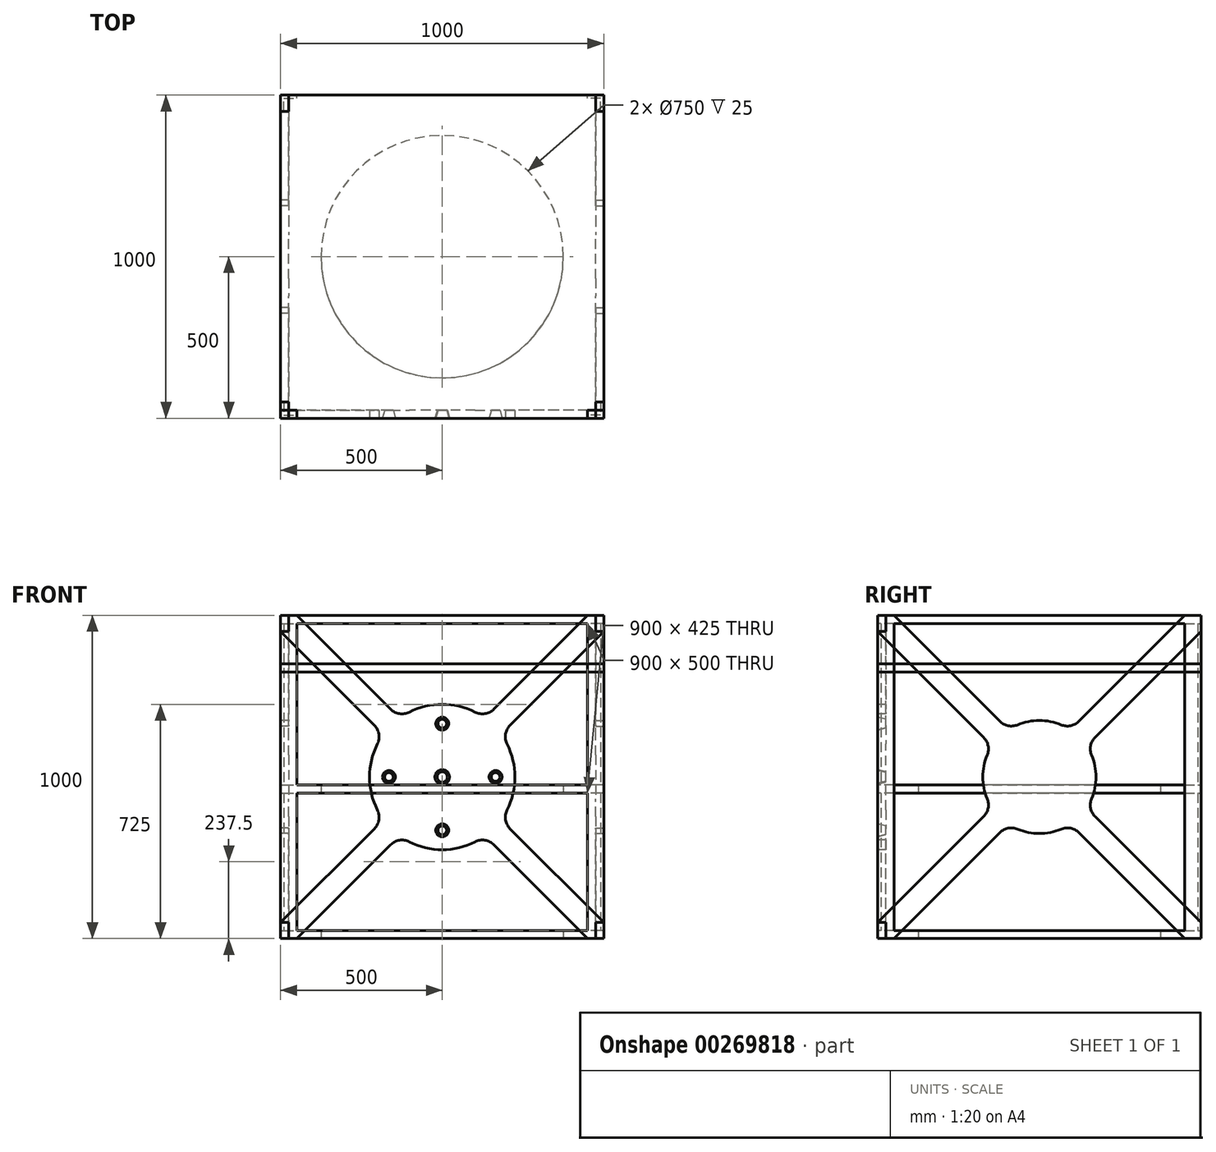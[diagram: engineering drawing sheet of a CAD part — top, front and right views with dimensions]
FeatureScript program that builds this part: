
annotation { "Feature Type Name" : "Feature", "Feature Type Description" : "" }
export const myFeature = defineFeature(function(context is Context, id is Id, definition is map)
    precondition{}
    {
        {
            var Q0;
            Q0=qCreatedBy(makeId("Top.planeOp"),FACE);
            var sketch = newSketch(context, id + "F0", { "sketchPlane" : qUnion([Q0])});
            skLineSegment(sketch, "E0.bottom", {"start": v(0, 0) * mm, "end": v(1000, 0) * mm});
            skLineSegment(sketch, "E0.top", {"start": v(0, -1000) * mm, "end": v(1000, -1000) * mm});
            skLineSegment(sketch, "E0.left", {"start": v(0, 0) * mm, "end": v(0, -1000) * mm});
            skLineSegment(sketch, "E0.right", {"start": v(1000, 0) * mm, "end": v(1000, -1000) * mm});
            skSolve(sketch);
        }
        {
            var Q0;
            Q0 = qSketchRegion(id + "F0", true);
            extrude(context, id + "F1", {"entities" : qUnion([Q0]), "depth" : 25 * mm});
        }
        {
            var Q0;
            Q0=makeQuery(id+"F1.opExtrude","CAP_FACE",FACE,{"disambiguationData":[OSD([sQuery(id+"F0.wireOp",EDGE,"E0.bottom"),sQuery(id+"F0.wireOp",EDGE,"E0.top"),sQuery(id+"F0.wireOp",EDGE,"E0.left"),sQuery(id+"F0.wireOp",EDGE,"E0.right")])],"isStart":false});
            var sketch = newSketch(context, id + "F2", { "sketchPlane" : qUnion([Q0])});
            skLineSegment(sketch, "E1", {"start": v(0, -1000) * mm, "end": v(0, -950) * mm});
            skLineSegment(sketch, "E2", {"start": v(0, -950) * mm, "end": v(10, -950) * mm});
            skLineSegment(sketch, "E3", {"start": v(10, -950) * mm, "end": v(10, -990) * mm});
            skLineSegment(sketch, "E4", {"start": v(10, -990) * mm, "end": v(50, -990) * mm});
            skLineSegment(sketch, "E5", {"start": v(50, -990) * mm, "end": v(50, -1000) * mm});
            skLineSegment(sketch, "E6", {"start": v(50, -1000) * mm, "end": v(0, -1000) * mm});
            skLineSegment(sketch, "E7", {"start": v(0, -500) * mm, "end": v(1000, -500) * mm, "construction": true});
            skLineSegment(sketch, "E8.MirrorCS", {"start": v(50, 0) * mm, "end": v(0, 0) * mm});
            skLineSegment(sketch, "E9.MirrorCS", {"start": v(50, -10) * mm, "end": v(50, 0) * mm});
            skLineSegment(sketch, "E10.MirrorCS", {"start": v(10, -10) * mm, "end": v(50, -10) * mm});
            skLineSegment(sketch, "E11.MirrorCS", {"start": v(10, -50) * mm, "end": v(10, -10) * mm});
            skLineSegment(sketch, "E12.MirrorCS", {"start": v(0, -50) * mm, "end": v(10, -50) * mm});
            skLineSegment(sketch, "E13.MirrorCS", {"start": v(0, 0) * mm, "end": v(0, -50) * mm});
            skLineSegment(sketch, "E14", {"start": v(500, 0) * mm, "end": v(500, -1000) * mm, "construction": true});
            skLineSegment(sketch, "E15.MirrorCS", {"start": v(950, -990) * mm, "end": v(950, -1000) * mm});
            skLineSegment(sketch, "E16.MirrorCS", {"start": v(990, -990) * mm, "end": v(950, -990) * mm});
            skLineSegment(sketch, "E17.MirrorCS", {"start": v(990, -950) * mm, "end": v(990, -990) * mm});
            skLineSegment(sketch, "E18.MirrorCS", {"start": v(1000, -950) * mm, "end": v(990, -950) * mm});
            skLineSegment(sketch, "E19.MirrorCS", {"start": v(1000, -1000) * mm, "end": v(1000, -950) * mm});
            skLineSegment(sketch, "E20.MirrorCS", {"start": v(950, -1000) * mm, "end": v(1000, -1000) * mm});
            skLineSegment(sketch, "E21.MirrorCS", {"start": v(1000, 0) * mm, "end": v(1000, -50) * mm});
            skLineSegment(sketch, "E22.MirrorCS", {"start": v(990, -10) * mm, "end": v(950, -10) * mm});
            skLineSegment(sketch, "E23.MirrorCS", {"start": v(950, 0) * mm, "end": v(1000, 0) * mm});
            skLineSegment(sketch, "E24.MirrorCS", {"start": v(1000, -50) * mm, "end": v(990, -50) * mm});
            skLineSegment(sketch, "E25.MirrorCS", {"start": v(990, -50) * mm, "end": v(990, -10) * mm});
            skLineSegment(sketch, "E26.MirrorCS", {"start": v(950, -10) * mm, "end": v(950, 0) * mm});
            skSolve(sketch);
        }
        {
            var Q0;
            Q0 = qSketchRegion(id + "F2", true);
            extrude(context, id + "F3", {"entities" : qUnion([Q0]), "operationType" : NewBodyOperationType.ADD, "depth" : 950 * mm});
        }
        {
            var Q0;
            Q0=qCreatedBy(makeId("Top.planeOp"),FACE);
            cPlane(context, id + "F4", {"entities" : qUnion([Q0]), "cplaneType" : CPlaneType.OFFSET, "offset" : 450 * mm, "width" : 150 * mm, "height" : 150 * mm});
        }
        {
            var Q0;
            Q0=qCreatedBy(id+"F4.planeOp",FACE);
            var sketch = newSketch(context, id + "F5", { "sketchPlane" : qUnion([Q0])});
            skLineSegment(sketch, "E27.bottom", {"start": v(0, 0) * mm, "end": v(998.65, 0) * mm});
            skLineSegment(sketch, "E27.top", {"start": v(0, -1000) * mm, "end": v(998.65, -1000) * mm});
            skLineSegment(sketch, "E27.left", {"start": v(0, 0) * mm, "end": v(0, -1000) * mm});
            skLineSegment(sketch, "E27.right", {"start": v(998.65, 0) * mm, "end": v(998.65, -1000) * mm});
            skSolve(sketch);
        }
        {
            var Q0;
            Q0 = qSketchRegion(id + "F5", true);
            extrude(context, id + "F6", {"entities" : qUnion([Q0]), "operationType" : NewBodyOperationType.ADD, "depth" : 25 * mm});
        }
        {
            var Q0;
            Q0=qCreatedBy(id+"F4.planeOp",FACE);
            cPlane(context, id + "F7", {"entities" : qUnion([Q0]), "cplaneType" : CPlaneType.OFFSET, "offset" : 400 * mm, "width" : 150 * mm, "height" : 150 * mm});
        }
        {
            var Q0;
            Q0=qCreatedBy(id+"F7.planeOp",FACE);
            var sketch = newSketch(context, id + "F8", { "sketchPlane" : qUnion([Q0])});
            skLineSegment(sketch, "E28.bottom", {"start": v(0, 0) * mm, "end": v(1000, 0) * mm});
            skLineSegment(sketch, "E28.top", {"start": v(0, -1000) * mm, "end": v(1000, -1000) * mm});
            skLineSegment(sketch, "E28.left", {"start": v(0, 0) * mm, "end": v(0, -1000) * mm});
            skLineSegment(sketch, "E28.right", {"start": v(1000, 0) * mm, "end": v(1000, -1000) * mm});
            skSolve(sketch);
        }
        {
            var Q0;
            Q0 = qSketchRegion(id + "F8", true);
            extrude(context, id + "F9", {"entities" : qUnion([Q0]), "oppositeDirection" : true, "depth" : 25 * mm});
        }
        {
            var Q0;
            Q0=makeQuery(id+"F3.opExtrude","CAP_FACE",FACE,{"disambiguationData":[OSD([sQuery(id+"F2.wireOp",EDGE,"E8.MirrorCS"),sQuery(id+"F2.wireOp",EDGE,"E9.MirrorCS"),sQuery(id+"F2.wireOp",EDGE,"E10.MirrorCS"),sQuery(id+"F2.wireOp",EDGE,"E11.MirrorCS"),sQuery(id+"F2.wireOp",EDGE,"E12.MirrorCS"),sQuery(id+"F2.wireOp",EDGE,"E13.MirrorCS")])],"isStart":false});
            var sketch = newSketch(context, id + "F10", { "sketchPlane" : qUnion([Q0])});
            skLineSegment(sketch, "E29.bottom", {"start": v(0, 0) * mm, "end": v(1000, 0) * mm});
            skLineSegment(sketch, "E29.top", {"start": v(0, -1000) * mm, "end": v(1000, -1000) * mm});
            skLineSegment(sketch, "E29.left", {"start": v(0, 0) * mm, "end": v(0, -1000) * mm});
            skLineSegment(sketch, "E29.right", {"start": v(1000, 0) * mm, "end": v(1000, -1000) * mm});
            skSolve(sketch);
        }
        {
            var Q0;
            Q0 = qSketchRegion(id + "F10", true);
            extrude(context, id + "F11", {"entities" : qUnion([Q0]), "operationType" : NewBodyOperationType.ADD, "depth" : 25 * mm});
        }
        {
            var Q0;
            Q0=makeQuery(id+"F1.opExtrude","CAP_FACE",FACE,{"disambiguationData":[OSD([sQuery(id+"F0.wireOp",EDGE,"E0.bottom"),sQuery(id+"F0.wireOp",EDGE,"E0.top"),sQuery(id+"F0.wireOp",EDGE,"E0.left"),sQuery(id+"F0.wireOp",EDGE,"E0.right")])],"isStart":true});
            var sketch = newSketch(context, id + "F12", { "sketchPlane" : qUnion([Q0])});
            skCircle(sketch, "E30", {"center": v(500, 500) * mm, "radius": 375 * mm});
            skSolve(sketch);
        }
        {
            var Q0;
            Q0 = qSketchRegion(id + "F12", true);
            extrude(context, id + "F13", {"entities" : qUnion([Q0]), "operationType" : NewBodyOperationType.REMOVE, "oppositeDirection" : true, "depth" : 592 * mm});
        }
        {
            var Q0;
            Q0=makeQuery(id+"F11.boolean.opBoolean","MERGE",FACE,{"derivedFrom":[makeQuery(id+"F6.boolean.opBoolean","MERGE",FACE,{"derivedFrom":[makeQuery(id+"F3.boolean.opBoolean","MERGE",FACE,{"derivedFrom":[makeQuery(id+"F1.opExtrude","SWEPT_FACE",FACE,{"disambiguationData":[OSD([sQuery(id+"F0.wireOp",EDGE,"E0.top")])]}),makeQuery(id+"F3.opExtrude","SWEPT_FACE",FACE,{"disambiguationData":[OSD([sQuery(id+"F2.wireOp",EDGE,"E6")])]}),makeQuery(id+"F3.opExtrude","SWEPT_FACE",FACE,{"disambiguationData":[OSD([sQuery(id+"F2.wireOp",EDGE,"E20.MirrorCS")])]})]}),makeQuery(id+"F6.opExtrude","SWEPT_FACE",FACE,{"disambiguationData":[OSD([sQuery(id+"F5.wireOp",EDGE,"E27.top")])]})]}),makeQuery(id+"F11.opExtrude","SWEPT_FACE",FACE,{"disambiguationData":[OSD([sQuery(id+"F10.wireOp",EDGE,"E29.top")])]})]});
            var sketch = newSketch(context, id + "F14", { "sketchPlane" : qUnion([Q0])});
            skLineSegment(sketch, "E31", {"start": v(1000, 0) * mm, "end": v(1000, 50) * mm});
            skLineSegment(sketch, "E32", {"start": v(1000, 50) * mm, "end": v(709.85, 340.15) * mm});
            skLineSegment(sketch, "E33", {"start": v(0, 1000) * mm, "end": v(0, 950) * mm});
            skLineSegment(sketch, "E34", {"start": v(0, 950) * mm, "end": v(290.15, 659.85) * mm});
            skLineSegment(sketch, "E35", {"start": v(1000, 0) * mm, "end": v(950, 0) * mm});
            skLineSegment(sketch, "E36", {"start": v(50, 1000) * mm, "end": v(0, 1000) * mm});
            skLineSegment(sketch, "E37", {"start": v(1000, 1000) * mm, "end": v(950, 1000) * mm});
            skLineSegment(sketch, "E38", {"start": v(950, 1000) * mm, "end": v(659.85, 709.85) * mm});
            skLineSegment(sketch, "E39", {"start": v(0, 50) * mm, "end": v(0, 0) * mm});
            skLineSegment(sketch, "E40", {"start": v(0, 0) * mm, "end": v(50, 0) * mm});
            skLineSegment(sketch, "E41", {"start": v(50, 0) * mm, "end": v(340.15, 290.15) * mm});
            skLineSegment(sketch, "E42", {"start": v(1000, 950) * mm, "end": v(1000, 1000) * mm});
            skPoint(sketch, "E43.centerSnap0", {"position": v(500, 475) * mm});
            skArc(sketch, "E44", {"start": v(299.38, 601.86) * mm, "mid": v(275, 500) * mm, "end": v(299.38, 398.14) * mm});
            skLineSegment(sketch, "E45.trimOffspring", {"start": v(290.15, 340.15) * mm, "end": v(0, 50) * mm});
            skLineSegment(sketch, "E46.trimOffspring", {"start": v(340.15, 709.85) * mm, "end": v(50, 1000) * mm});
            skLineSegment(sketch, "E47.trimOffspring", {"start": v(659.85, 290.15) * mm, "end": v(950, 0) * mm});
            skLineSegment(sketch, "E48.trimOffspring", {"start": v(709.85, 659.85) * mm, "end": v(1000, 950) * mm});
            skArc(sketch, "E49.trimOffspring", {"start": v(601.86, 700.62) * mm, "mid": v(500, 725) * mm, "end": v(398.14, 700.62) * mm});
            skArc(sketch, "E50.trimOffspring", {"start": v(700.62, 398.14) * mm, "mid": v(725, 500) * mm, "end": v(700.62, 601.86) * mm});
            skArc(sketch, "E51.trimOffspring", {"start": v(398.14, 299.38) * mm, "mid": v(500, 275) * mm, "end": v(601.86, 299.38) * mm});
            skPoint(sketch, "E52.visualSharp", {"position": v(682.12, 367.88) * mm});
            skArc(sketch, "E52.filletArc", {"start": v(700.62, 398.14) * mm, "mid": v(695.83, 367.65) * mm, "end": v(709.85, 340.15) * mm});
            skPoint(sketch, "E53.visualSharp", {"position": v(632.12, 317.88) * mm});
            skArc(sketch, "E53.filletArc", {"start": v(659.85, 290.15) * mm, "mid": v(632.35, 304.17) * mm, "end": v(601.86, 299.38) * mm});
            skPoint(sketch, "E54.visualSharp", {"position": v(367.88, 317.88) * mm});
            skArc(sketch, "E54.filletArc", {"start": v(398.14, 299.38) * mm, "mid": v(367.65, 304.17) * mm, "end": v(340.15, 290.15) * mm});
            skPoint(sketch, "E55.visualSharp", {"position": v(317.88, 367.88) * mm});
            skArc(sketch, "E55.filletArc", {"start": v(290.15, 340.15) * mm, "mid": v(304.17, 367.65) * mm, "end": v(299.38, 398.14) * mm});
            skPoint(sketch, "E56.visualSharp", {"position": v(317.88, 632.12) * mm});
            skArc(sketch, "E56.filletArc", {"start": v(299.38, 601.86) * mm, "mid": v(304.17, 632.35) * mm, "end": v(290.15, 659.85) * mm});
            skPoint(sketch, "E57.visualSharp", {"position": v(367.88, 682.12) * mm});
            skArc(sketch, "E57.filletArc", {"start": v(340.15, 709.85) * mm, "mid": v(367.65, 695.83) * mm, "end": v(398.14, 700.62) * mm});
            skPoint(sketch, "E58.visualSharp", {"position": v(632.12, 682.12) * mm});
            skArc(sketch, "E58.filletArc", {"start": v(601.86, 700.62) * mm, "mid": v(632.35, 695.83) * mm, "end": v(659.85, 709.85) * mm});
            skPoint(sketch, "E59.visualSharp", {"position": v(682.12, 632.12) * mm});
            skArc(sketch, "E59.filletArc", {"start": v(709.85, 659.85) * mm, "mid": v(695.83, 632.35) * mm, "end": v(700.62, 601.86) * mm});
            skSolve(sketch);
        }
        {
            var Q0;
            Q0 = qSketchRegion(id + "F14", true);
            extrude(context, id + "F15", {"entities" : qUnion([Q0]), "oppositeDirection" : true, "depth" : 25 * mm});
        }
        {
            var Q0;
            Q0=makeQuery(id+"F15.opExtrude","CAP_FACE",FACE,{"disambiguationData":[OSD([sQuery(id+"F14.wireOp",EDGE,"E31"),sQuery(id+"F14.wireOp",EDGE,"E32"),sQuery(id+"F14.wireOp",EDGE,"E33"),sQuery(id+"F14.wireOp",EDGE,"E34"),sQuery(id+"F14.wireOp",EDGE,"E35"),sQuery(id+"F14.wireOp",EDGE,"E36"),sQuery(id+"F14.wireOp",EDGE,"E37"),sQuery(id+"F14.wireOp",EDGE,"E38"),sQuery(id+"F14.wireOp",EDGE,"E39"),sQuery(id+"F14.wireOp",EDGE,"E40"),sQuery(id+"F14.wireOp",EDGE,"E41"),sQuery(id+"F14.wireOp",EDGE,"E42"),sQuery(id+"F14.wireOp",EDGE,"E44"),sQuery(id+"F14.wireOp",EDGE,"E45.trimOffspring"),sQuery(id+"F14.wireOp",EDGE,"E46.trimOffspring"),sQuery(id+"F14.wireOp",EDGE,"E47.trimOffspring"),sQuery(id+"F14.wireOp",EDGE,"E48.trimOffspring"),sQuery(id+"F14.wireOp",EDGE,"E49.trimOffspring"),sQuery(id+"F14.wireOp",EDGE,"E50.trimOffspring"),sQuery(id+"F14.wireOp",EDGE,"E51.trimOffspring"),sQuery(id+"F14.wireOp",EDGE,"E52.filletArc"),sQuery(id+"F14.wireOp",EDGE,"E53.filletArc"),sQuery(id+"F14.wireOp",EDGE,"E54.filletArc"),sQuery(id+"F14.wireOp",EDGE,"E55.filletArc"),sQuery(id+"F14.wireOp",EDGE,"E56.filletArc"),sQuery(id+"F14.wireOp",EDGE,"E57.filletArc"),sQuery(id+"F14.wireOp",EDGE,"E58.filletArc"),sQuery(id+"F14.wireOp",EDGE,"E59.filletArc")])],"isStart":true});
            var sketch = newSketch(context, id + "F16", { "sketchPlane" : qUnion([Q0])});
            skCircle(sketch, "E60", {"center": v(500, 500) * mm, "radius": 22.5 * mm});
            skCircle(sketch, "E61", {"center": v(500, 665) * mm, "radius": 20 * mm});
            skCircle(sketch, "E62.1.0", {"center": v(335, 500) * mm, "radius": 20 * mm});
            skCircle(sketch, "E62.2.0", {"center": v(500, 335) * mm, "radius": 20 * mm});
            skCircle(sketch, "E62.3.0", {"center": v(665, 500) * mm, "radius": 20 * mm});
            skSolve(sketch);
        }
        {
            var Q0;
            Q0 = qSketchRegion(id + "F16", true);
            extrude(context, id + "F17", {"entities" : qUnion([Q0]), "operationType" : NewBodyOperationType.REMOVE, "oppositeDirection" : true, "depth" : 25 * mm, "hasDraft" : true, "draftAngle" : 15 * degree, "draftPullDirection" : true});
        }
        {
            var Q0;
            Q0=makeQuery(id+"F11.boolean.opBoolean","MERGE",FACE,{"derivedFrom":[makeQuery(id+"F3.boolean.opBoolean","MERGE",FACE,{"derivedFrom":[makeQuery(id+"F1.opExtrude","SWEPT_FACE",FACE,{"disambiguationData":[OSD([sQuery(id+"F0.wireOp",EDGE,"E0.right")])]}),makeQuery(id+"F3.opExtrude","SWEPT_FACE",FACE,{"disambiguationData":[OSD([sQuery(id+"F2.wireOp",EDGE,"E19.MirrorCS")])]}),makeQuery(id+"F3.opExtrude","SWEPT_FACE",FACE,{"disambiguationData":[OSD([sQuery(id+"F2.wireOp",EDGE,"E21.MirrorCS")])]})]}),makeQuery(id+"F11.opExtrude","SWEPT_FACE",FACE,{"disambiguationData":[OSD([sQuery(id+"F10.wireOp",EDGE,"E29.right")])]})]});
            var sketch = newSketch(context, id + "F18", { "sketchPlane" : qUnion([Q0])});
            skLineSegment(sketch, "E63", {"start": v(-1000, 1000) * mm, "end": v(-950, 1000) * mm});
            skLineSegment(sketch, "E64", {"start": v(-950, 1000) * mm, "end": v(-622.2, 672.2) * mm});
            skLineSegment(sketch, "E65", {"start": v(0, 50) * mm, "end": v(0, 0) * mm});
            skLineSegment(sketch, "E66", {"start": v(0, 0) * mm, "end": v(-50, 0) * mm});
            skLineSegment(sketch, "E67", {"start": v(-50, 0) * mm, "end": v(-377.8, 327.8) * mm});
            skLineSegment(sketch, "E68", {"start": v(-1000, 950) * mm, "end": v(-1000, 1000) * mm});
            skLineSegment(sketch, "E69", {"start": v(0, 1000) * mm, "end": v(-50, 1000) * mm});
            skLineSegment(sketch, "E70", {"start": v(-50, 1000) * mm, "end": v(-377.8, 672.2) * mm});
            skLineSegment(sketch, "E71", {"start": v(-1000, 50) * mm, "end": v(-1000, 0) * mm});
            skLineSegment(sketch, "E72", {"start": v(-1000, 0) * mm, "end": v(-950, 0) * mm});
            skLineSegment(sketch, "E73", {"start": v(-950, 0) * mm, "end": v(-622.2, 327.8) * mm});
            skLineSegment(sketch, "E74", {"start": v(0, 950) * mm, "end": v(0, 1000) * mm});
            skArc(sketch, "E75", {"start": v(-338.56, 432.45) * mm, "mid": v(-325, 500) * mm, "end": v(-338.56, 567.55) * mm});
            skLineSegment(sketch, "E76.trimOffspring", {"start": v(-327.8, 377.8) * mm, "end": v(0, 50) * mm});
            skLineSegment(sketch, "E77.trimOffspring", {"start": v(-672.2, 377.8) * mm, "end": v(-1000, 50) * mm});
            skLineSegment(sketch, "E78.trimOffspring", {"start": v(-327.8, 622.2) * mm, "end": v(0, 950) * mm});
            skLineSegment(sketch, "E79.trimOffspring", {"start": v(-672.2, 622.2) * mm, "end": v(-1000, 950) * mm});
            skArc(sketch, "E80.trimOffspring", {"start": v(-432.45, 661.44) * mm, "mid": v(-500, 675) * mm, "end": v(-567.55, 661.44) * mm});
            skArc(sketch, "E81.trimOffspring", {"start": v(-661.44, 567.55) * mm, "mid": v(-675, 500) * mm, "end": v(-661.44, 432.45) * mm});
            skArc(sketch, "E82.trimOffspring", {"start": v(-567.55, 338.56) * mm, "mid": v(-500, 325) * mm, "end": v(-432.45, 338.56) * mm});
            skPoint(sketch, "E83.visualSharp", {"position": v(-596.2, 646.2) * mm});
            skArc(sketch, "E83.filletArc", {"start": v(-622.2, 672.2) * mm, "mid": v(-596.52, 658.5) * mm, "end": v(-567.55, 661.44) * mm});
            skPoint(sketch, "E84.visualSharp", {"position": v(-403.8, 646.2) * mm});
            skArc(sketch, "E84.filletArc", {"start": v(-432.45, 661.44) * mm, "mid": v(-403.48, 658.5) * mm, "end": v(-377.8, 672.2) * mm});
            skPoint(sketch, "E85.visualSharp", {"position": v(-353.8, 596.2) * mm});
            skArc(sketch, "E85.filletArc", {"start": v(-327.8, 622.2) * mm, "mid": v(-341.5, 596.52) * mm, "end": v(-338.56, 567.55) * mm});
            skPoint(sketch, "E86.visualSharp", {"position": v(-353.8, 403.8) * mm});
            skArc(sketch, "E86.filletArc", {"start": v(-338.56, 432.45) * mm, "mid": v(-341.5, 403.48) * mm, "end": v(-327.8, 377.8) * mm});
            skPoint(sketch, "E87.visualSharp", {"position": v(-403.8, 353.8) * mm});
            skArc(sketch, "E87.filletArc", {"start": v(-377.8, 327.8) * mm, "mid": v(-403.48, 341.5) * mm, "end": v(-432.45, 338.56) * mm});
            skPoint(sketch, "E88.visualSharp", {"position": v(-596.2, 353.8) * mm});
            skArc(sketch, "E88.filletArc", {"start": v(-567.55, 338.56) * mm, "mid": v(-596.52, 341.5) * mm, "end": v(-622.2, 327.8) * mm});
            skPoint(sketch, "E89.visualSharp", {"position": v(-646.2, 403.8) * mm});
            skArc(sketch, "E89.filletArc", {"start": v(-672.2, 377.8) * mm, "mid": v(-658.5, 403.48) * mm, "end": v(-661.44, 432.45) * mm});
            skPoint(sketch, "E90.visualSharp", {"position": v(-646.2, 596.2) * mm});
            skArc(sketch, "E90.filletArc", {"start": v(-661.44, 567.55) * mm, "mid": v(-658.5, 596.52) * mm, "end": v(-672.2, 622.2) * mm});
            skSolve(sketch);
        }
        {
            var Q0;
            Q0 = qSketchRegion(id + "F18", true);
            extrude(context, id + "F19", {"entities" : qUnion([Q0]), "oppositeDirection" : true, "depth" : 25 * mm});
        }
        {
            var Q0;
            Q0=qCreatedBy(makeId("Right.planeOp"),FACE);
            cPlane(context, id + "F20", {"entities" : qUnion([Q0]), "cplaneType" : CPlaneType.OFFSET, "offset" : 500 * mm, "width" : 150 * mm, "height" : 150 * mm});
        }
        {
            var Q0;
            Q0=makeQuery(id+"F19.opExtrude","SWEPT_BODY",BODY,{"disambiguationData":[OSD([sQuery(id+"F18.wireOp",EDGE,"E63"),sQuery(id+"F18.wireOp",EDGE,"E64"),sQuery(id+"F18.wireOp",EDGE,"E65"),sQuery(id+"F18.wireOp",EDGE,"E66"),sQuery(id+"F18.wireOp",EDGE,"E67"),sQuery(id+"F18.wireOp",EDGE,"E68"),sQuery(id+"F18.wireOp",EDGE,"E69"),sQuery(id+"F18.wireOp",EDGE,"E70"),sQuery(id+"F18.wireOp",EDGE,"E71"),sQuery(id+"F18.wireOp",EDGE,"E72"),sQuery(id+"F18.wireOp",EDGE,"E73"),sQuery(id+"F18.wireOp",EDGE,"E74"),sQuery(id+"F18.wireOp",EDGE,"E75"),sQuery(id+"F18.wireOp",EDGE,"E76.trimOffspring"),sQuery(id+"F18.wireOp",EDGE,"E77.trimOffspring"),sQuery(id+"F18.wireOp",EDGE,"E78.trimOffspring"),sQuery(id+"F18.wireOp",EDGE,"E79.trimOffspring"),sQuery(id+"F18.wireOp",EDGE,"E80.trimOffspring"),sQuery(id+"F18.wireOp",EDGE,"E81.trimOffspring"),sQuery(id+"F18.wireOp",EDGE,"E82.trimOffspring"),sQuery(id+"F18.wireOp",EDGE,"E83.filletArc"),sQuery(id+"F18.wireOp",EDGE,"E84.filletArc"),sQuery(id+"F18.wireOp",EDGE,"E85.filletArc"),sQuery(id+"F18.wireOp",EDGE,"E86.filletArc"),sQuery(id+"F18.wireOp",EDGE,"E87.filletArc"),sQuery(id+"F18.wireOp",EDGE,"E88.filletArc"),sQuery(id+"F18.wireOp",EDGE,"E89.filletArc"),sQuery(id+"F18.wireOp",EDGE,"E90.filletArc")])]});
            var Q1;
            Q1=qCreatedBy(id+"F20.planeOp",FACE);
            mirror(context, id + "F21", {"entities" : qUnion([Q0]), "mirrorPlane" : qUnion([Q1])});
        }
    });
